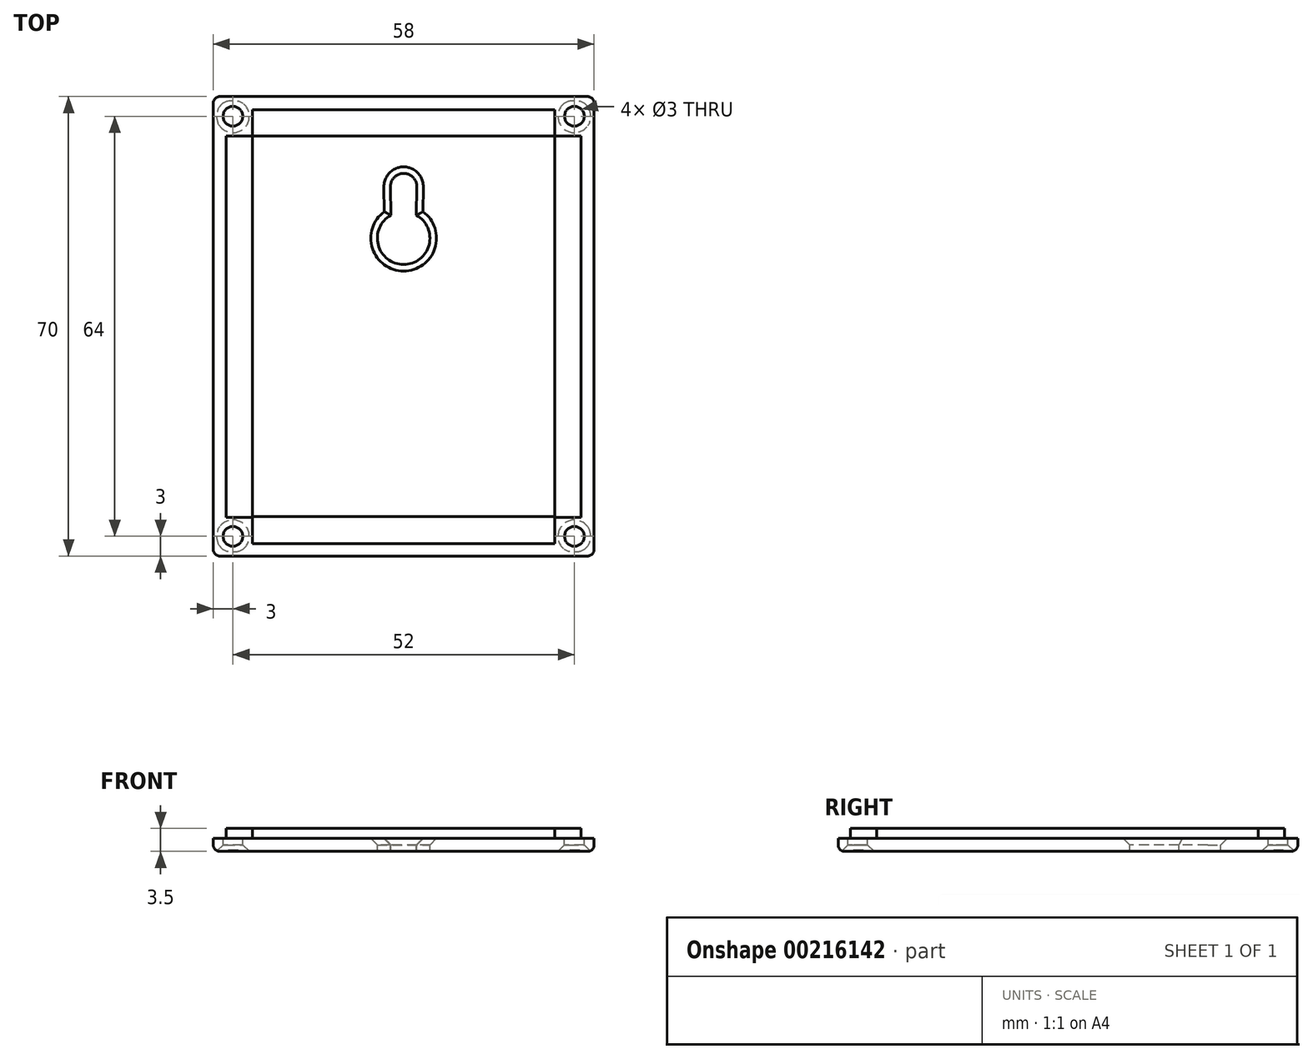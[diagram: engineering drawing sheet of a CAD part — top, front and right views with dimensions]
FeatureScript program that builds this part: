
annotation { "Feature Type Name" : "Feature", "Feature Type Description" : "" }
export const myFeature = defineFeature(function(context is Context, id is Id, definition is map)
    precondition{}
    {
        {
            var Q0;
            Q0=qCreatedBy(makeId("Top.planeOp"),FACE);
            var sketch = newSketch(context, id + "F0", { "sketchPlane" : qUnion([Q0])});
            skLineSegment(sketch, "E0.bottom", {"start": v(29, -35) * mm, "end": v(-29, -35) * mm});
            skLineSegment(sketch, "E0.top", {"start": v(29, 35) * mm, "end": v(-29, 35) * mm});
            skLineSegment(sketch, "E0.left", {"start": v(29, -35) * mm, "end": v(29, 35) * mm});
            skLineSegment(sketch, "E0.right", {"start": v(-29, -35) * mm, "end": v(-29, 35) * mm});
            skPoint(sketch, "E0.middle", {"position": v(0, 0) * mm});
            skLineSegment(sketch, "E1.bottom", {"start": v(27, -33.1) * mm, "end": v(-27, -33.1) * mm});
            skLineSegment(sketch, "E1.right", {"start": v(-27, -33.1) * mm, "end": v(-27, 33) * mm});
            skLineSegment(sketch, "E2.top", {"start": v(-27, 29) * mm, "end": v(-23, 29) * mm});
            skLineSegment(sketch, "E2.right", {"start": v(-23, 33) * mm, "end": v(-23, 29) * mm});
            skLineSegment(sketch, "E3.MirrorCS", {"start": v(23, 33) * mm, "end": v(23, 29) * mm});
            skLineSegment(sketch, "E4.MirrorCS", {"start": v(27, 29) * mm, "end": v(23, 29) * mm});
            skLineSegment(sketch, "E5.MirrorCS", {"start": v(-27, 33) * mm, "end": v(27, 33) * mm});
            skLineSegment(sketch, "E6.MirrorCS", {"start": v(27, -33.1) * mm, "end": v(27, 33) * mm});
            skLineSegment(sketch, "E7.MirrorCS", {"start": v(27, -29.1) * mm, "end": v(22.99, -29.1) * mm});
            skLineSegment(sketch, "E8.MirrorCS", {"start": v(22.99, -33.1) * mm, "end": v(22.99, -29.1) * mm});
            skLineSegment(sketch, "E9.MirrorCS", {"start": v(-23, -33.1) * mm, "end": v(-23, -29.1) * mm});
            skLineSegment(sketch, "E10.MirrorCS", {"start": v(-27, -29.1) * mm, "end": v(-23, -29.1) * mm});
            skCircle(sketch, "E11", {"center": v(-26, 32) * mm, "radius": 1.5 * mm});
            skCircle(sketch, "E12.MirrorC", {"center": v(26, 32) * mm, "radius": 1.5 * mm});
            skCircle(sketch, "E13.MirrorC", {"center": v(-26, -32) * mm, "radius": 1.5 * mm});
            skCircle(sketch, "E14.MirrorC", {"center": v(26, -32) * mm, "radius": 1.5 * mm});
            skArc(sketch, "E15", {"start": v(-1.95, 16.91) * mm, "mid": v(0, 9.42) * mm, "end": v(1.95, 16.91) * mm});
            skArc(sketch, "E16", {"start": v(2, 21.27) * mm, "mid": v(0, 23.3) * mm, "end": v(-2, 21.27) * mm});
            skLineSegment(sketch, "E17", {"start": v(-2, 21.27) * mm, "end": v(-1.95, 16.91) * mm});
            skLineSegment(sketch, "E18.MirrorCS", {"start": v(2, 21.27) * mm, "end": v(1.95, 16.91) * mm});
            skSolve(sketch);
        }
        {
            var Q0;
            Q0 = qSketchRegion(id + "F0", true);
            var Q1;
            {var subQ3=sQuery(id+"F0.wireOp",EDGE,"E9.MirrorCS");Q1=makeQuery(id+"F0.imprint","IMPRINT",FACE,{"disambiguationData":[TD([[makeQuery(id+"F0.imprint","IMPRINT",EDGE,{"derivedFrom":subQ3}),1.0]])]});}
            var Q2;
            {var subQ9=sQuery(id+"F0.wireOp",EDGE,"E2.top");Q2=makeQuery(id+"F0.imprint","IMPRINT",FACE,{"disambiguationData":[TD([[makeQuery(id+"F0.imprint","IMPRINT",EDGE,{"derivedFrom":subQ9}),-1.0]])]});}
            var Q3;
            {var subQ4=sQuery(id+"F0.wireOp",EDGE,"E7.MirrorCS");Q3=makeQuery(id+"F0.imprint","IMPRINT",FACE,{"disambiguationData":[TD([[makeQuery(id+"F0.imprint","IMPRINT",EDGE,{"derivedFrom":subQ4}),1.0]])]});}
            var Q4;
            {var subQ3=sQuery(id+"F0.wireOp",EDGE,"E2.top");Q4=makeQuery(id+"F0.imprint","IMPRINT",FACE,{"disambiguationData":[TD([[makeQuery(id+"F0.imprint","IMPRINT",EDGE,{"derivedFrom":subQ3}),1.0]])]});}
            var Q5;
            {var subQ0=sQuery(id+"F0.wireOp",EDGE,"E3.MirrorCS");Q5=makeQuery(id+"F0.imprint","IMPRINT",FACE,{"disambiguationData":[TD([[makeQuery(id+"F0.imprint","IMPRINT",EDGE,{"derivedFrom":subQ0}),1.0]])]});}
            extrude(context, id + "F1", {"entities" : qUnion([Q0, Q1, Q2, Q3, Q4, Q5]), "oppositeDirection" : true, "depth" : 2 * mm});
        }
        {
            var Q0;
            {var subQ9=sQuery(id+"F0.wireOp",EDGE,"E2.top");Q0=makeQuery(id+"F0.imprint","IMPRINT",FACE,{"disambiguationData":[TD([[makeQuery(id+"F0.imprint","IMPRINT",EDGE,{"derivedFrom":subQ9}),-1.0]])]});}
            extrude(context, id + "F2", {"entities" : qUnion([Q0]), "depth" : 1.5 * mm});
        }
        {
            var Q0;
            Q0=makeQuery(id+"F1.opExtrude","CAP_EDGE",EDGE,{"disambiguationData":[OSD([sQuery(id+"F0.wireOp",EDGE,"E12.MirrorC")])],"isStart":false});
            var Q1;
            Q1=makeQuery(id+"F1.opExtrude","CAP_EDGE",EDGE,{"disambiguationData":[OSD([sQuery(id+"F0.wireOp",EDGE,"E11")])],"isStart":false});
            var Q2;
            Q2=makeQuery(id+"F1.opExtrude","CAP_EDGE",EDGE,{"disambiguationData":[OSD([sQuery(id+"F0.wireOp",EDGE,"E14.MirrorC")])],"isStart":false});
            var Q3;
            Q3=makeQuery(id+"F1.opExtrude","CAP_EDGE",EDGE,{"disambiguationData":[OSD([sQuery(id+"F0.wireOp",EDGE,"E13.MirrorC")])],"isStart":false});
            chamfer(context, id + "F3", {"entities" : qUnion([Q0, Q1, Q2, Q3]), "width" : 1 * mm, "tangentPropagation" : true});
        }
        {
            var Q0;
            Q0=makeQuery(id+"F1.opExtrude","CAP_EDGE",EDGE,{"disambiguationData":[OSD([sQuery(id+"F0.wireOp",EDGE,"E0.bottom")])],"isStart":false});
            var Q1;
            Q1=makeQuery(id+"F1.opExtrude","CAP_EDGE",EDGE,{"disambiguationData":[OSD([sQuery(id+"F0.wireOp",EDGE,"E0.right")])],"isStart":false});
            var Q2;
            Q2=makeQuery(id+"F1.opExtrude","CAP_EDGE",EDGE,{"disambiguationData":[OSD([sQuery(id+"F0.wireOp",EDGE,"E0.left")])],"isStart":false});
            var Q3;
            Q3=makeQuery(id+"F1.opExtrude","CAP_EDGE",EDGE,{"disambiguationData":[OSD([sQuery(id+"F0.wireOp",EDGE,"E0.top")])],"isStart":false});
            var Q4;
            Q4=makeQuery(id+"F1.opExtrude","SWEPT_EDGE",EDGE,{"disambiguationData":[OSD([sQuery(id+"F0.wireOp",EDGE,"E0.top"),sQuery(id+"F0.wireOp",EDGE,"E0.right")])]});
            var Q5;
            Q5=makeQuery(id+"F1.opExtrude","SWEPT_EDGE",EDGE,{"disambiguationData":[OSD([sQuery(id+"F0.wireOp",EDGE,"E0.top"),sQuery(id+"F0.wireOp",EDGE,"E0.left")])]});
            var Q6;
            Q6=makeQuery(id+"F1.opExtrude","SWEPT_EDGE",EDGE,{"disambiguationData":[OSD([sQuery(id+"F0.wireOp",EDGE,"E0.bottom"),sQuery(id+"F0.wireOp",EDGE,"E0.left")])]});
            var Q7;
            Q7=makeQuery(id+"F1.opExtrude","SWEPT_EDGE",EDGE,{"disambiguationData":[OSD([sQuery(id+"F0.wireOp",EDGE,"E0.bottom"),sQuery(id+"F0.wireOp",EDGE,"E0.right")])]});
            fillet(context, id + "F4", {"entities" : qUnion([Q0, Q1, Q2, Q3, Q4, Q5, Q6, Q7]), "radius" : 1 * mm, "tangentPropagation" : true, "allowEdgeOverflow" : false});
        }
        {
            var Q0;
            Q0=makeQuery(id+"F2.opExtrude","CAP_FACE",FACE,{"disambiguationData":[OSD([sQuery(id+"F0.wireOp",EDGE,"E1.bottom"),sQuery(id+"F0.wireOp",EDGE,"E1.right"),sQuery(id+"F0.wireOp",EDGE,"E2.top"),sQuery(id+"F0.wireOp",EDGE,"E2.right"),sQuery(id+"F0.wireOp",EDGE,"E3.MirrorCS"),sQuery(id+"F0.wireOp",EDGE,"E4.MirrorCS"),sQuery(id+"F0.wireOp",EDGE,"E5.MirrorCS"),sQuery(id+"F0.wireOp",EDGE,"E6.MirrorCS"),sQuery(id+"F0.wireOp",EDGE,"E7.MirrorCS"),sQuery(id+"F0.wireOp",EDGE,"E8.MirrorCS"),sQuery(id+"F0.wireOp",EDGE,"E9.MirrorCS"),sQuery(id+"F0.wireOp",EDGE,"E10.MirrorCS")])],"isStart":false});
            var sketch = newSketch(context, id + "F5", { "sketchPlane" : qUnion([Q0])});
            skLineSegment(sketch, "E19.bottom", {"start": v(-23, 29) * mm, "end": v(23, 29) * mm});
            skLineSegment(sketch, "E19.top", {"start": v(-23, -29) * mm, "end": v(23, -29) * mm});
            skLineSegment(sketch, "E19.left", {"start": v(-23, 29) * mm, "end": v(-23, -29) * mm});
            skLineSegment(sketch, "E19.right", {"start": v(23, 29) * mm, "end": v(23, -29) * mm});
            skPoint(sketch, "E19.middle", {"position": v(0, 0) * mm});
            skSolve(sketch);
        }
        {
            var Q0;
            Q0=makeQuery(id+"F5.imprint","IMPRINT",FACE,{"disambiguationData":[TD([[makeQuery(id+"F5.imprint","IMPRINT",EDGE,{"derivedFrom":sQuery(id+"F5.wireOp",EDGE,"E19.top")}),1.0]])]});
            extrude(context, id + "F6", {"entities" : qUnion([Q0]), "operationType" : NewBodyOperationType.REMOVE, "oppositeDirection" : true, "depth" : 1.5 * mm});
        }
        {
            var Q0;
            Q0=makeQuery(id+"F1.opExtrude","CAP_EDGE",EDGE,{"disambiguationData":[OSD([sQuery(id+"F0.wireOp",EDGE,"E16")])],"isStart":true});
            var Q1;
            Q1=makeQuery(id+"F1.opExtrude","CAP_EDGE",EDGE,{"disambiguationData":[OSD([sQuery(id+"F0.wireOp",EDGE,"E17")])],"isStart":true});
            var Q2;
            Q2=makeQuery(id+"F1.opExtrude","CAP_EDGE",EDGE,{"disambiguationData":[OSD([sQuery(id+"F0.wireOp",EDGE,"E15")])],"isStart":true});
            var Q3;
            Q3=makeQuery(id+"F1.opExtrude","CAP_EDGE",EDGE,{"disambiguationData":[OSD([sQuery(id+"F0.wireOp",EDGE,"E18.MirrorCS")])],"isStart":true});
            chamfer(context, id + "F7", {"entities" : qUnion([Q0, Q1, Q2, Q3]), "width" : 1 * mm, "tangentPropagation" : true});
        }
    });
